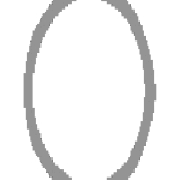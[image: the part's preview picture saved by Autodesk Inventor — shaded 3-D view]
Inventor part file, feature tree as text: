
AUTODESK INVENTOR PART (.ipt)
format: ipt  version: 2021 (Build 250183000, 183)  size: 111,616 bytes
history: native  units: in
note: dims shown in document units (in); Inventor stores cm internally (conversion verified against a paired STEP export)
features: other x4, sketch x3, plane x1
ambient origin geometry x8: Origin, YZ Plane, XZ Plane, XY Plane, X Axis, Y Axis, Z Axis, Center Point
bodies: Solid1 (feature_tree), Body (feature_tree)
feature tree (8):
  other  "Driven Length"
  other  "Frame Generator"
  other  "Start Plane"
  other  "End Plane"
  sketch  "Sketch"  dims[d2=20.0811in d4=-0.0in d5=20.0811in d6=0.12in d7=0.0in d8=90.0deg d9=20.0811in]
  sketch  "Sketch2"  dims[d0=1.0in]
  plane  "Work Plane3"
  sketch  "Sketch3"  dims[d1=0.065in]
